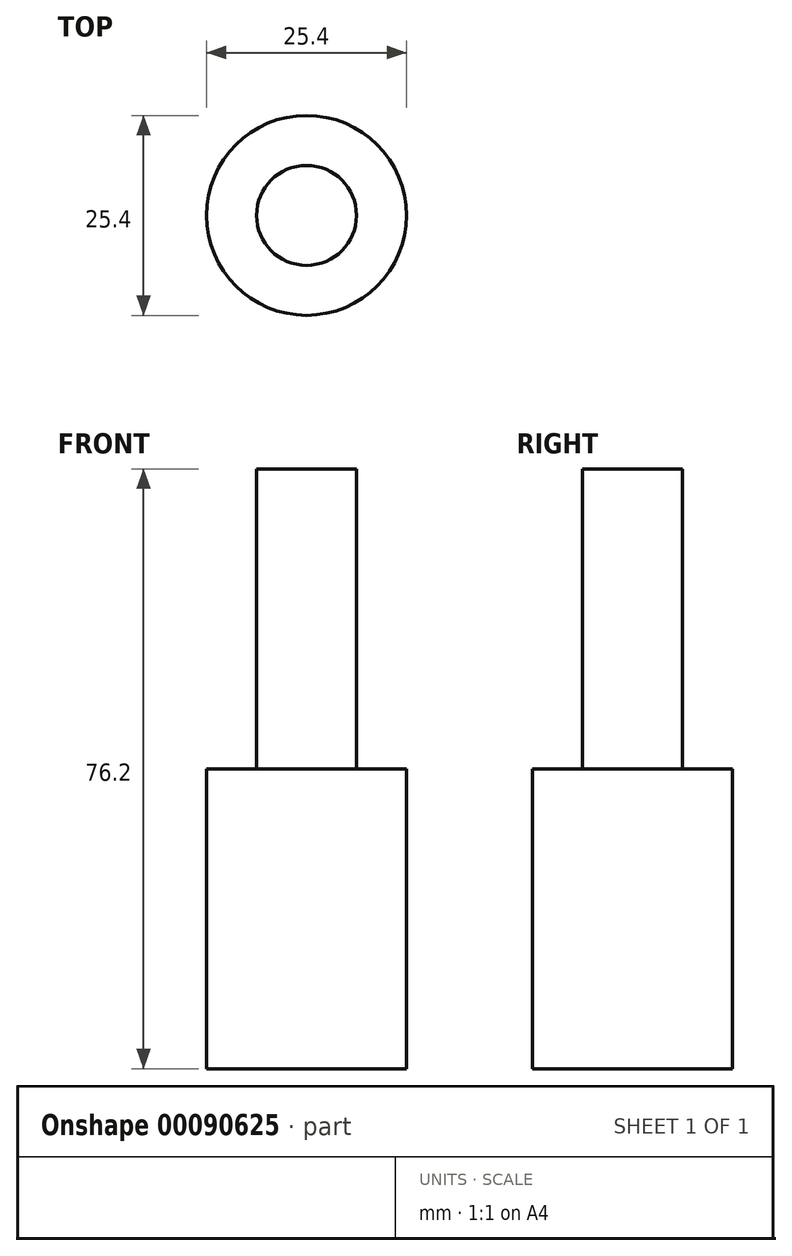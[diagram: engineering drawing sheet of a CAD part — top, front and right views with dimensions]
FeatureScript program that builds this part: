
annotation { "Feature Type Name" : "Feature", "Feature Type Description" : "" }
export const myFeature = defineFeature(function(context is Context, id is Id, definition is map)
    precondition{}
    {
        {
            var Q0;
            Q0=qCreatedBy(makeId("Top.planeOp"),FACE);
            var sketch = newSketch(context, id + "F0", { "sketchPlane" : qUnion([Q0])});
            skCircle(sketch, "E0", {"center": v(0, 0) * mm, "radius": 6.35 * mm});
            skSolve(sketch);
        }
        {
            var Q0;
            Q0=qCreatedBy(makeId("Top.planeOp"),FACE);
            var sketch = newSketch(context, id + "F1", { "sketchPlane" : qUnion([Q0])});
            skCircle(sketch, "E1", {"center": v(0, 0) * mm, "radius": 12.7 * mm});
            skSolve(sketch);
        }
        {
            var Q0;
            Q0 = qSketchRegion(id + "F0", true);
            var Q1;
            Q1=makeQuery(id+"F0.imprint","IMPRINT",FACE,{"disambiguationData":[TD([[makeQuery(id+"F0.imprint","IMPRINT",EDGE,{"derivedFrom":sQuery(id+"F0.wireOp",EDGE,"E0")}),1.0]])]});
            extrude(context, id + "F2", {"entities" : qUnion([Q0, Q1]), "depth" : 76.2 * mm});
        }
        {
            var Q0;
            Q0=makeQuery(id+"F1.imprint","IMPRINT",FACE,{"disambiguationData":[TD([[makeQuery(id+"F1.imprint","IMPRINT",EDGE,{"derivedFrom":sQuery(id+"F1.wireOp",EDGE,"E1")}),1.0]])]});
            extrude(context, id + "F3", {"entities" : qUnion([Q0]), "operationType" : NewBodyOperationType.ADD, "depth" : 38.1 * mm});
        }
    });
